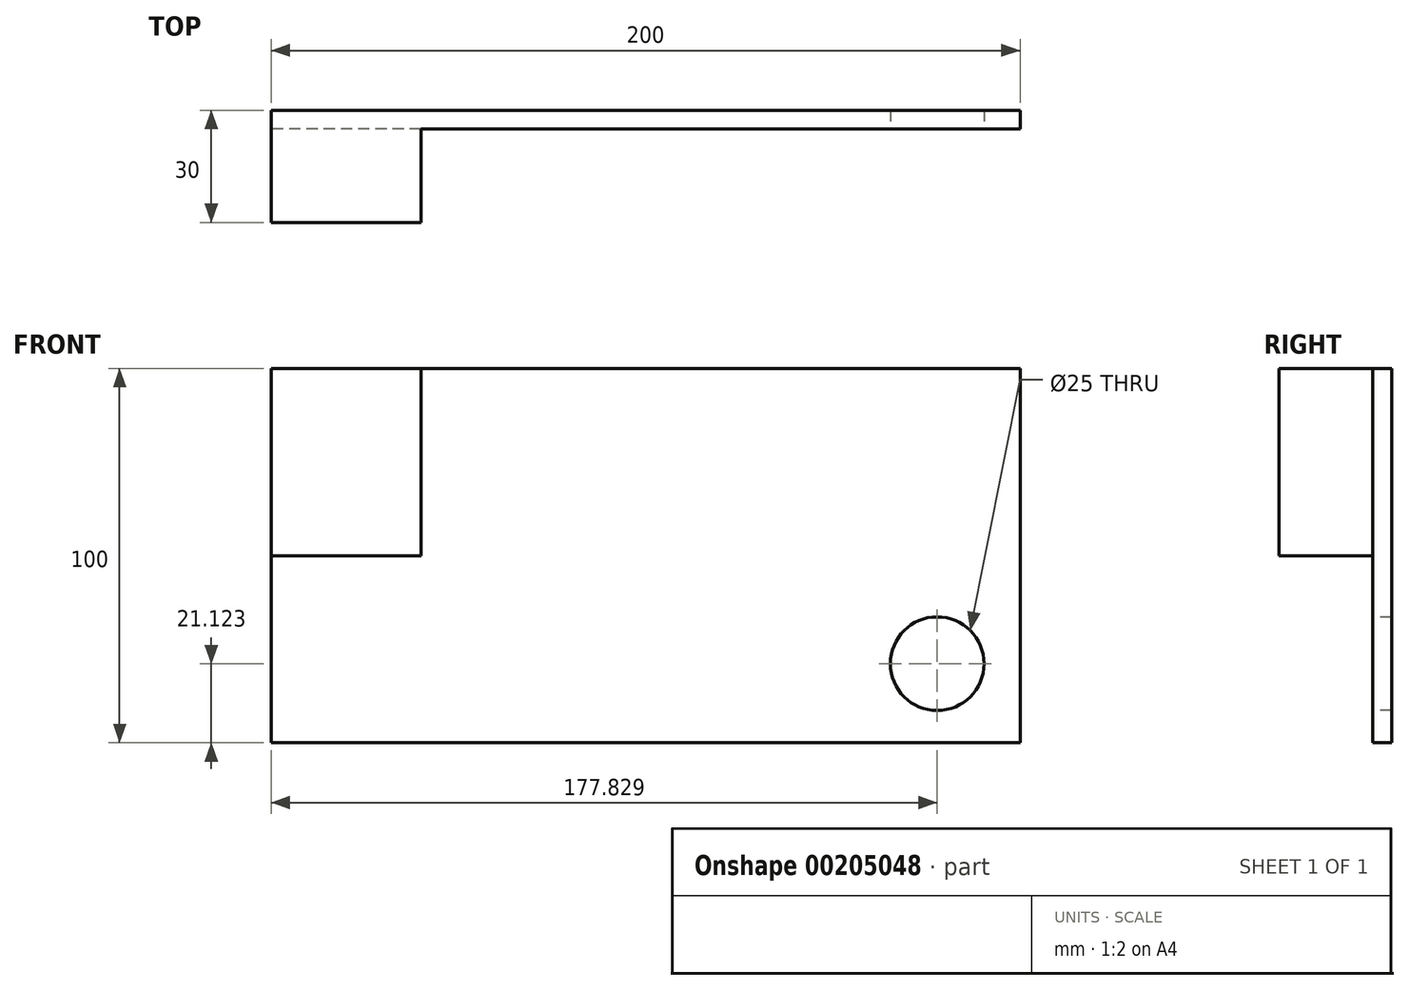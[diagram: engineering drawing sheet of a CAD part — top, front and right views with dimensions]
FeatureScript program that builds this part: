
annotation { "Feature Type Name" : "Feature", "Feature Type Description" : "" }
export const myFeature = defineFeature(function(context is Context, id is Id, definition is map)
    precondition{}
    {
        {
            var Q0;
            Q0=qCreatedBy(makeId("Front.planeOp"),FACE);
            var sketch = newSketch(context, id + "F0", { "sketchPlane" : qUnion([Q0])});
            skLineSegment(sketch, "E0.bottom", {"start": v(-99.22, 52.73) * mm, "end": v(100.78, 52.73) * mm});
            skLineSegment(sketch, "E0.top", {"start": v(-99.22, -47.27) * mm, "end": v(100.78, -47.27) * mm});
            skLineSegment(sketch, "E0.left", {"start": v(-99.22, 52.73) * mm, "end": v(-99.22, -47.27) * mm});
            skLineSegment(sketch, "E0.right", {"start": v(100.78, 52.73) * mm, "end": v(100.78, -47.27) * mm});
            skSolve(sketch);
        }
        {
            var Q0;
            Q0 = qSketchRegion(id + "F0", true);
            extrude(context, id + "F1", {"entities" : qUnion([Q0]), "depth" : 5 * mm});
        }
        {
            var Q0;
            Q0=makeQuery(id+"F1.opExtrude","CAP_FACE",FACE,{"disambiguationData":[OSD([sQuery(id+"F0.wireOp",EDGE,"E0.bottom"),sQuery(id+"F0.wireOp",EDGE,"E0.top"),sQuery(id+"F0.wireOp",EDGE,"E0.left"),sQuery(id+"F0.wireOp",EDGE,"E0.right")])],"isStart":false});
            var sketch = newSketch(context, id + "F2", { "sketchPlane" : qUnion([Q0])});
            skLineSegment(sketch, "E1", {"start": v(-59.22, 52.73) * mm, "end": v(-59.22, 2.73) * mm});
            skLineSegment(sketch, "E2", {"start": v(-59.22, 2.73) * mm, "end": v(-99.22, 2.73) * mm});
            skSolve(sketch);
        }
        {
            var Q0;
            Q0 = qSketchRegion(id + "F2", true);
            var Q1;
            {var subQ0=sQuery(id+"F2.wireOp",EDGE,"E1");Q1=makeQuery(id+"F2.imprint","IMPRINT",FACE,{"disambiguationData":[TD([[makeQuery(id+"F2.imprint","IMPRINT",EDGE,{"derivedFrom":subQ0}),-1.0]])]});}
            extrude(context, id + "F3", {"entities" : qUnion([Q0, Q1]), "operationType" : NewBodyOperationType.ADD, "depth" : 25 * mm});
        }
        {
            var Q0;
            Q0=makeQuery(id+"F1.opExtrude","CAP_FACE",FACE,{"disambiguationData":[OSD([sQuery(id+"F0.wireOp",EDGE,"E0.bottom"),sQuery(id+"F0.wireOp",EDGE,"E0.top"),sQuery(id+"F0.wireOp",EDGE,"E0.left"),sQuery(id+"F0.wireOp",EDGE,"E0.right")])],"isStart":false});
            var sketch = newSketch(context, id + "F4", { "sketchPlane" : qUnion([Q0])});
            skPoint(sketch, "E3", {"position": v(78.6, -26.15) * mm});
            skSolve(sketch);
        }
        {
            var Q0;
            Q0=sQuery(id+"F4.wireOp",VERTEX,"E3");
            var Q1;
            Q1=makeQuery(id+"F1.opExtrude","SWEPT_BODY",BODY,{"disambiguationData":[OSD([sQuery(id+"F0.wireOp",EDGE,"E0.bottom"),sQuery(id+"F0.wireOp",EDGE,"E0.top"),sQuery(id+"F0.wireOp",EDGE,"E0.left"),sQuery(id+"F0.wireOp",EDGE,"E0.right")])]});
            hole(context, id + "F5", {"style" : HoleStyle.SIMPLE, "endStyle" : HoleEndStyle.THROUGH, "standardTappedOrClearance" : lookupTablePath({ "standard" : "ISO", "size" : "25", "type" : "Drilled" }), "standardBlindInLast" : lookupTablePath({ "standard" : "ISO", "size" : "25", "type" : "Drilled" }), "holeDiameter" : 25 * mm, "locations" : qUnion([Q0]), "scope" : qUnion([Q1]), "isTappedThrough" : true});
        }
    });
